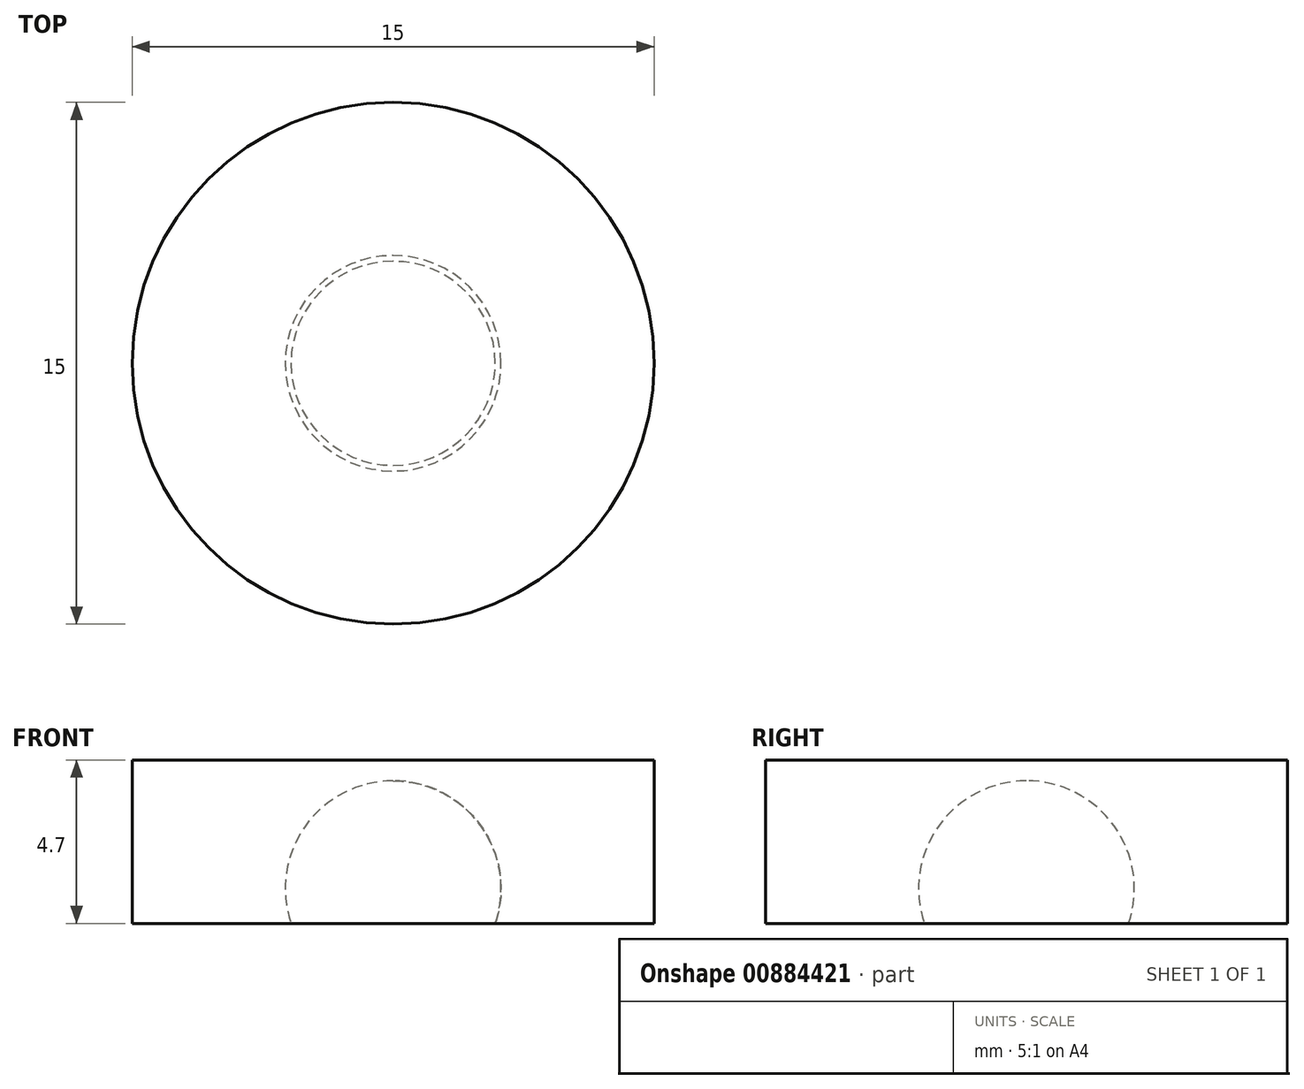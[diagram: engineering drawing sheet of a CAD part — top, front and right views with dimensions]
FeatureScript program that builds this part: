
annotation { "Feature Type Name" : "Feature", "Feature Type Description" : "" }
export const myFeature = defineFeature(function(context is Context, id is Id, definition is map)
    precondition{}
    {
        {
            var Q0;
            Q0=qCreatedBy(makeId("Front.planeOp"),FACE);
            var sketch = newSketch(context, id + "F0", { "sketchPlane" : qUnion([Q0])});
            skArc(sketch, "E0", {"start": v(2.93, 0) * mm, "mid": v(2.52, 2.8) * mm, "end": v(0, 4.1) * mm});
            skLineSegment(sketch, "E1", {"start": v(2.93, 0) * mm, "end": v(7.5, 0) * mm});
            skLineSegment(sketch, "E2", {"start": v(7.5, 0) * mm, "end": v(7.5, 4.7) * mm});
            skLineSegment(sketch, "E3", {"start": v(7.5, 4.7) * mm, "end": v(0, 4.7) * mm});
            skLineSegment(sketch, "E4", {"start": v(0, 4.7) * mm, "end": v(0, 4.1) * mm});
            skLineSegment(sketch, "E5", {"start": v(0, 0) * mm, "end": v(0, 12.09) * mm, "construction": true});
            skSolve(sketch);
        }
        {
            var Q0;
            Q0 = qSketchRegion(id + "F0", true);
            var Q1;
            Q1=sQuery(id+"F0.wireOp",EDGE,"E5");
            revolve(context, id + "F1", {"surfaceOperationType" : NewSurfaceOperationType.NEW, "entities" : qUnion([Q0]), "axis" : qUnion([Q1]), "revolveType" : RevolveType.FULL});
        }
    });
